# Revit family: HUNTER_A2C-Decoder Metal Pedestal
name_source: partatom
category: Electrical Equipment
revit_build: Autodesk Revit 2017 (Build: 20171027_0315(x64)
units: mm (PartAtom-declared; Revit-internal decimal feet)

## family parameters
Always vertical = Yes
Cut with Voids When Loaded = No
OmniClass Number = 23.35.25.21
Panel Configuration = One Column
Part Type = Panelboard
Room Calculation Point = No
Round Connector Dimension = Use Diameter
Shared = Yes
Work Plane-Based = Yes

## types (2) — shared parameters
Assembly Code = D5090900
Current = 2 A
Decoders = Hunter ICD Decoders / Expandable Up to 225 stations
Default Elevation = 1219 mm
Expansion Module = A2C-D75 (75 Stations plug-in) Expansion Module
Input Voltage = 120 V
Keynote = 328423.04
Manufacturer = Hunter® Industries
Number of Sensor Inputs = Flow Input and sensor decoder
Output Voltage = 24 V
Panel Type = Modular Decoder
Power = 240 VA
Power Factor = 1
Protection Rating = IP44
Sensor Input = 3 Clik, 1 Solar Sync, and 6 Flow Sensor
Stations = 75-225 Decoder Stations
Transformer Output = 24VAC, 4.0A
Type Comments = Hunter’s Flagship Controller
Type Image = <None>
URL = https://www.hunterindustries.com

## per-type parameters (varying)
| type | ACC-1200 | ACC-1200-SS | Description | Model | Pedestal Material |
| A2C-75D-M with ACC-PED | Yes | No | 75-station base model expandable , Metal enclosure and pedestal | ACC-75D-M with ACC-PED Expandable Up to 225 stations with Decoders | Hunter® Metal Grey |
| A2C-75D-SS with PED SS | No | Yes | 75-station base model expandable , Stainless steel enclosure and pedestal | ACC-75D-SS with PED-SS Expandable Up to 225 stations with Decoders | Hunter® Stainless Steel |

## geometry (parser evidence)
native form markers: Sweep x7
no freeform markers — native parametric forms only
